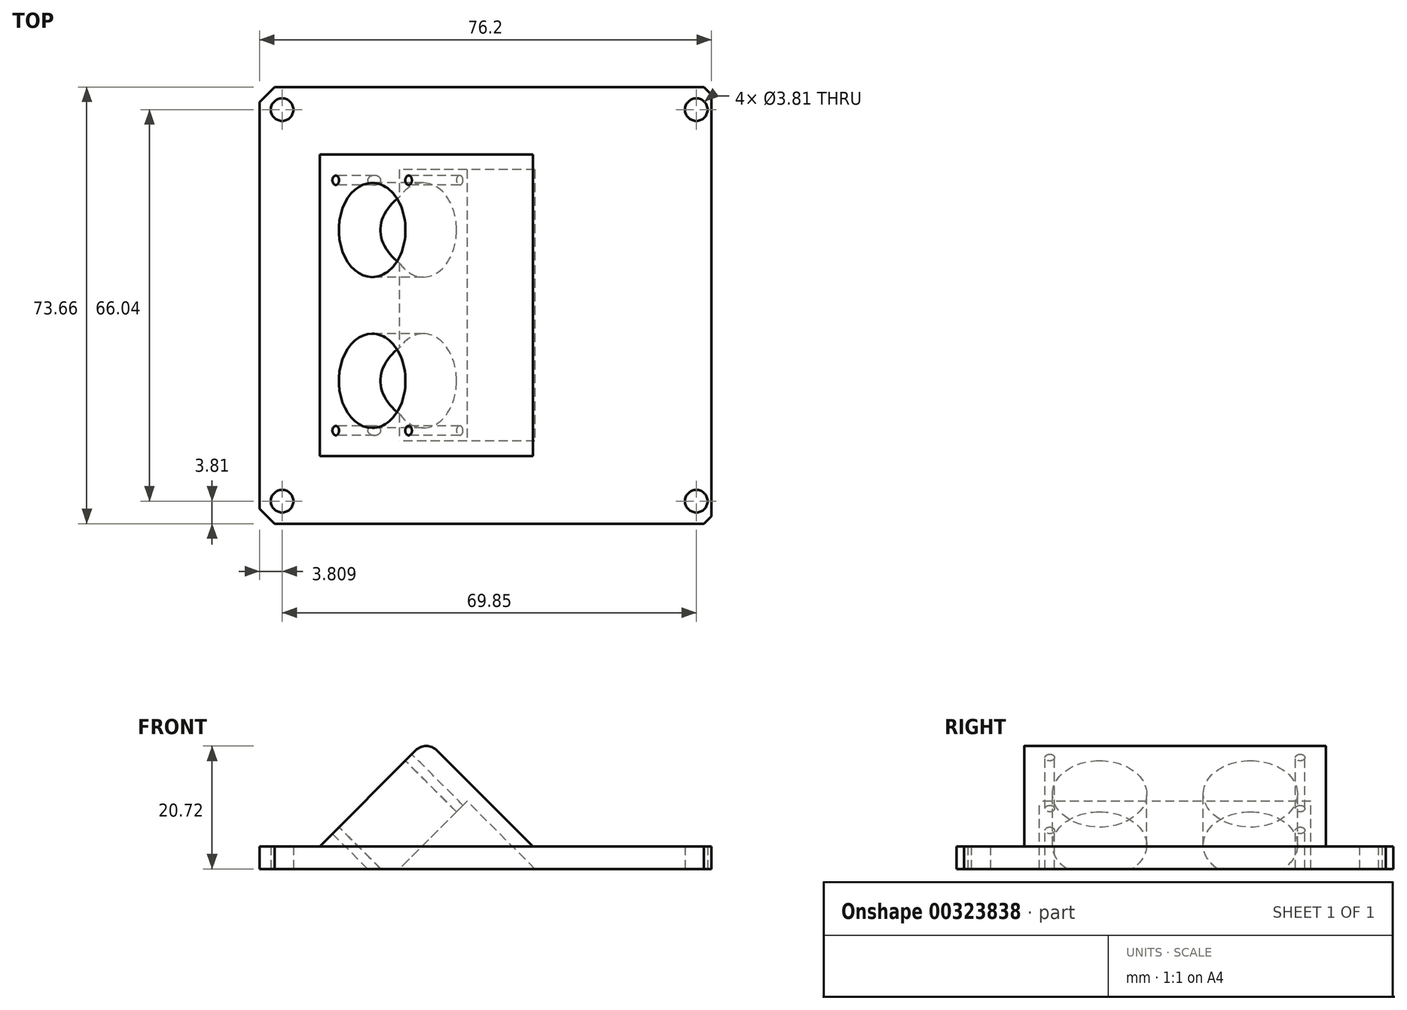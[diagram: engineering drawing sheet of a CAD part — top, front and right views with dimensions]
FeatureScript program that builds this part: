
annotation { "Feature Type Name" : "Feature", "Feature Type Description" : "" }
export const myFeature = defineFeature(function(context is Context, id is Id, definition is map)
    precondition{}
    {
        {
            var Q0;
            Q0=qCreatedBy(makeId("Top.planeOp"),FACE);
            var sketch = newSketch(context, id + "F0", { "sketchPlane" : qUnion([Q0])});
            skLineSegment(sketch, "E0.bottom", {"start": v(-80.1, 87.1) * mm, "end": v(-3.9, 87.1) * mm});
            skLineSegment(sketch, "E0.top", {"start": v(-80.1, 13.44) * mm, "end": v(-3.9, 13.44) * mm});
            skLineSegment(sketch, "E0.left", {"start": v(-80.1, 87.1) * mm, "end": v(-80.1, 13.44) * mm});
            skLineSegment(sketch, "E0.right", {"start": v(-3.9, 87.1) * mm, "end": v(-3.9, 13.44) * mm});
            skCircle(sketch, "E1", {"center": v(-76.28, 83.29) * mm, "radius": 1.9 * mm});
            skCircle(sketch, "E2", {"center": v(-6.43, 83.29) * mm, "radius": 1.9 * mm});
            skCircle(sketch, "E3", {"center": v(-6.43, 17.25) * mm, "radius": 1.9 * mm});
            skCircle(sketch, "E4", {"center": v(-76.28, 17.25) * mm, "radius": 1.9 * mm});
            skSolve(sketch);
        }
        {
            var Q0;
            Q0=makeQuery(id+"F0.imprint","IMPRINT",FACE,{"disambiguationData":[TD([[makeQuery(id+"F0.imprint","IMPRINT",EDGE,{"derivedFrom":sQuery(id+"F0.wireOp",EDGE,"E0.bottom")}),-1.0]])]});
            extrude(context, id + "F1", {"entities" : qUnion([Q0]), "depth" : 3.8 * mm});
        }
        {
            var Q0;
            Q0=makeQuery(id+"F1.opExtrude","SWEPT_EDGE",EDGE,{"disambiguationData":[OSD([sQuery(id+"F0.wireOp",EDGE,"E0.top"),sQuery(id+"F0.wireOp",EDGE,"E0.right")])]});
            var Q1;
            Q1=makeQuery(id+"F1.opExtrude","SWEPT_EDGE",EDGE,{"disambiguationData":[OSD([sQuery(id+"F0.wireOp",EDGE,"E0.bottom"),sQuery(id+"F0.wireOp",EDGE,"E0.right")])]});
            chamfer(context, id + "F2", {"entities" : qUnion([Q0, Q1]), "width" : 1.27 * mm, "tangentPropagation" : true});
        }
        {
            var Q0;
            Q0=makeQuery(id+"F1.opExtrude","SWEPT_EDGE",EDGE,{"disambiguationData":[OSD([sQuery(id+"F0.wireOp",EDGE,"E0.top"),sQuery(id+"F0.wireOp",EDGE,"E0.left")])]});
            var Q1;
            Q1=makeQuery(id+"F1.opExtrude","SWEPT_EDGE",EDGE,{"disambiguationData":[OSD([sQuery(id+"F0.wireOp",EDGE,"E0.bottom"),sQuery(id+"F0.wireOp",EDGE,"E0.left")])]});
            chamfer(context, id + "F3", {"entities" : qUnion([Q0, Q1]), "width" : 2.54 * mm, "tangentPropagation" : true});
        }
        {
            var Q0;
            Q0=makeQuery(id+"F1.opExtrude","SWEPT_FACE",FACE,{"disambiguationData":[OSD([sQuery(id+"F0.wireOp",EDGE,"E0.top")])]});
            var sketch = newSketch(context, id + "F4", { "sketchPlane" : qUnion([Q0])});
            skLineSegment(sketch, "E5", {"start": v(-69.93, 3.8) * mm, "end": v(-51.97, 21.77) * mm});
            skLineSegment(sketch, "E6", {"start": v(-51.97, 21.77) * mm, "end": v(-34, 3.8) * mm});
            skSolve(sketch);
        }
        {
            var Q0;
            {var subQ0=sQuery(id+"F4.wireOp",EDGE,"E5");Q0=makeQuery(id+"F4.imprint","IMPRINT",FACE,{"disambiguationData":[TD([[makeQuery(id+"F4.imprint","IMPRINT",EDGE,{"derivedFrom":subQ0}),-1.0]])]});}
            var Q1;
            Q1=makeQuery(id+"F1.opExtrude","SWEPT_FACE",FACE,{"disambiguationData":[OSD([sQuery(id+"F0.wireOp",EDGE,"E0.bottom")])]});
            extrude(context, id + "F5", {"entities" : qUnion([Q0]), "operationType" : NewBodyOperationType.ADD, "endBound" : BoundingType.UP_TO_SURFACE, "oppositeDirection" : true, "endBoundEntityFace" : qUnion([Q1]), "depth" : 25.4 * mm});
        }
        {
            var Q0;
            Q0=makeQuery(id+"F5.opExtrude","SWEPT_FACE",FACE,{"disambiguationData":[OSD([sQuery(id+"F4.wireOp",EDGE,"E5")])]});
            var sketch = newSketch(context, id + "F6", { "sketchPlane" : qUnion([Q0])});
            skCircle(sketch, "E7", {"center": v(-71.38, -25.57) * mm, "radius": 0.8 * mm});
            skCircle(sketch, "E8", {"center": v(-29.16, -25.57) * mm, "radius": 0.8 * mm});
            skCircle(sketch, "E9", {"center": v(-29.16, -42.94) * mm, "radius": 0.8 * mm});
            skCircle(sketch, "E10", {"center": v(-71.38, -42.94) * mm, "radius": 0.8 * mm});
            skCircle(sketch, "E11", {"center": v(-62.99, -34.26) * mm, "radius": 7.94 * mm});
            skCircle(sketch, "E12", {"center": v(-37.55, -34.26) * mm, "radius": 7.94 * mm});
            skSolve(sketch);
        }
        {
            var Q0;
            Q0=makeQuery(id+"F6.imprint","IMPRINT",FACE,{"disambiguationData":[TD([[makeQuery(id+"F6.imprint","IMPRINT",EDGE,{"derivedFrom":sQuery(id+"F6.wireOp",EDGE,"E11")}),1.0]])]});
            var Q1;
            Q1=makeQuery(id+"F6.imprint","IMPRINT",FACE,{"disambiguationData":[TD([[makeQuery(id+"F6.imprint","IMPRINT",EDGE,{"derivedFrom":sQuery(id+"F6.wireOp",EDGE,"E12")}),1.0]])]});
            var Q2;
            Q2=makeQuery(id+"F6.imprint","IMPRINT",FACE,{"disambiguationData":[TD([[makeQuery(id+"F6.imprint","IMPRINT",EDGE,{"derivedFrom":sQuery(id+"F6.wireOp",EDGE,"E8")}),1.0]])]});
            var Q3;
            Q3=makeQuery(id+"F6.imprint","IMPRINT",FACE,{"disambiguationData":[TD([[makeQuery(id+"F6.imprint","IMPRINT",EDGE,{"derivedFrom":sQuery(id+"F6.wireOp",EDGE,"E9")}),1.0]])]});
            var Q4;
            Q4=makeQuery(id+"F6.imprint","IMPRINT",FACE,{"disambiguationData":[TD([[makeQuery(id+"F6.imprint","IMPRINT",EDGE,{"derivedFrom":sQuery(id+"F6.wireOp",EDGE,"E10")}),1.0]])]});
            var Q5;
            Q5=makeQuery(id+"F6.imprint","IMPRINT",FACE,{"disambiguationData":[TD([[makeQuery(id+"F6.imprint","IMPRINT",EDGE,{"derivedFrom":sQuery(id+"F6.wireOp",EDGE,"E7")}),1.0]])]});
            extrude(context, id + "F7", {"entities" : qUnion([Q0, Q1, Q2, Q3, Q4, Q5]), "operationType" : NewBodyOperationType.REMOVE, "endBound" : BoundingType.THROUGH_ALL, "oppositeDirection" : true, "depth" : 25.4 * mm});
        }
        {
            var Q0;
            Q0=makeQuery(id+"F5.opExtrude","SWEPT_FACE",FACE,{"disambiguationData":[OSD([sQuery(id+"F4.wireOp",EDGE,"E5")])]});
            cPlane(context, id + "F8", {"entities" : qUnion([Q0]), "cplaneType" : CPlaneType.OFFSET, "offset" : 12.2 * mm, "oppositeDirection" : true, "width" : 152.4 * mm, "height" : 152.4 * mm});
        }
        {
            var Q0;
            Q0=qCreatedBy(id+"F8.planeOp",FACE);
            var sketch = newSketch(context, id + "F9", { "sketchPlane" : qUnion([Q0])});
            skCircle(sketch, "E13.0", {"center": v(-71.38, -25.57) * mm, "radius": 0.8 * mm});
            skCircle(sketch, "E14.0", {"center": v(-29.16, -25.57) * mm, "radius": 0.8 * mm});
            skCircle(sketch, "E15.0", {"center": v(-29.16, -42.94) * mm, "radius": 0.8 * mm});
            skCircle(sketch, "E16.0", {"center": v(-71.38, -42.94) * mm, "radius": 0.8 * mm});
            skLineSegment(sketch, "E17.bottom", {"start": v(-72.9, -24.05) * mm, "end": v(-27.63, -24.05) * mm});
            skLineSegment(sketch, "E17.top", {"start": v(-72.9, -44.47) * mm, "end": v(-27.63, -44.47) * mm});
            skLineSegment(sketch, "E17.left", {"start": v(-72.9, -24.05) * mm, "end": v(-72.9, -44.47) * mm});
            skLineSegment(sketch, "E17.right", {"start": v(-27.63, -24.05) * mm, "end": v(-27.63, -44.47) * mm});
            skLineSegment(sketch, "E18.0", {"start": v(-73.16, -23.8) * mm, "end": v(-27.38, -23.8) * mm});
            skLineSegment(sketch, "E18.1", {"start": v(-73.16, -23.8) * mm, "end": v(-73.16, -44.72) * mm});
            skLineSegment(sketch, "E18.2", {"start": v(-73.16, -44.72) * mm, "end": v(-27.38, -44.72) * mm});
            skLineSegment(sketch, "E18.3", {"start": v(-27.38, -23.8) * mm, "end": v(-27.38, -44.72) * mm});
            skSolve(sketch);
        }
        {
            var Q0;
            Q0=makeQuery(id+"F9.imprint","IMPRINT",FACE,{"disambiguationData":[TD([[makeQuery(id+"F9.imprint","IMPRINT",EDGE,{"derivedFrom":sQuery(id+"F9.wireOp",EDGE,"E17.bottom")}),1.0]])]});
            var Q1;
            Q1=makeQuery(id+"F9.imprint","IMPRINT",FACE,{"disambiguationData":[TD([[makeQuery(id+"F9.imprint","IMPRINT",EDGE,{"derivedFrom":sQuery(id+"F9.wireOp",EDGE,"E13.0")}),-1.0]])]});
            var Q2;
            Q2=makeQuery(id+"F9.imprint","IMPRINT",FACE,{"disambiguationData":[TD([[makeQuery(id+"F9.imprint","IMPRINT",EDGE,{"derivedFrom":sQuery(id+"F9.wireOp",EDGE,"E14.0")}),1.0]])]});
            var Q3;
            Q3=makeQuery(id+"F9.imprint","IMPRINT",FACE,{"disambiguationData":[TD([[makeQuery(id+"F9.imprint","IMPRINT",EDGE,{"derivedFrom":sQuery(id+"F9.wireOp",EDGE,"E15.0")}),1.0]])]});
            var Q4;
            Q4=makeQuery(id+"F9.imprint","IMPRINT",FACE,{"disambiguationData":[TD([[makeQuery(id+"F9.imprint","IMPRINT",EDGE,{"derivedFrom":sQuery(id+"F9.wireOp",EDGE,"E16.0")}),1.0]])]});
            var Q5;
            Q5=makeQuery(id+"F9.imprint","IMPRINT",FACE,{"disambiguationData":[TD([[makeQuery(id+"F9.imprint","IMPRINT",EDGE,{"derivedFrom":sQuery(id+"F9.wireOp",EDGE,"E13.0")}),1.0]])]});
            extrude(context, id + "F10", {"entities" : qUnion([Q0, Q1, Q2, Q3, Q4, Q5]), "operationType" : NewBodyOperationType.REMOVE, "oppositeDirection" : true, "depth" : 25.4 * mm});
        }
        {
            var Q0;
            Q0=makeQuery(id+"F1.opExtrude","SWEPT_FACE",FACE,{"disambiguationData":[OSD([sQuery(id+"F0.wireOp",EDGE,"E0.left")])]});
            var sketch = newSketch(context, id + "F11", { "sketchPlane" : qUnion([Q0])});
            skLineSegment(sketch, "E19.0", {"start": v(-73.16, 11.43) * mm, "end": v(-73.16, 0) * mm});
            skLineSegment(sketch, "E20.0", {"start": v(-27.38, 11.43) * mm, "end": v(-27.38, 0) * mm});
            skLineSegment(sketch, "E21", {"start": v(-94.18, 27.08) * mm, "end": v(-75.7, 27.08) * mm});
            skLineSegment(sketch, "E22", {"start": v(-75.7, 27.08) * mm, "end": v(-75.7, 3.81) * mm});
            skLineSegment(sketch, "E23", {"start": v(-75.7, 3.81) * mm, "end": v(-93.65, 3.81) * mm});
            skLineSegment(sketch, "E24", {"start": v(-93.65, 3.81) * mm, "end": v(-94.18, 27.08) * mm});
            skLineSegment(sketch, "E25", {"start": v(-50.27, 3.81) * mm, "end": v(-50.27, 21.74) * mm, "construction": true});
            skPoint(sketch, "E25.endSnap0", {"position": v(-50.27, 3.81) * mm});
            skLineSegment(sketch, "E26.MirrorCS", {"start": v(-6.36, 27.08) * mm, "end": v(-24.84, 27.08) * mm});
            skLineSegment(sketch, "E27.MirrorCS", {"start": v(-24.84, 27.08) * mm, "end": v(-24.84, 3.81) * mm});
            skLineSegment(sketch, "E28.MirrorCS", {"start": v(-24.84, 3.81) * mm, "end": v(-6.89, 3.81) * mm});
            skLineSegment(sketch, "E29.MirrorCS", {"start": v(-6.89, 3.81) * mm, "end": v(-6.36, 27.08) * mm});
            skSolve(sketch);
        }
        {
            var Q0;
            Q0=makeQuery(id+"F11.imprint","IMPRINT",FACE,{"disambiguationData":[TD([[makeQuery(id+"F11.imprint","IMPRINT",EDGE,{"derivedFrom":sQuery(id+"F11.wireOp",EDGE,"E21")}),-1.0]])]});
            var Q1;
            Q1=makeQuery(id+"F11.imprint","IMPRINT",FACE,{"disambiguationData":[TD([[makeQuery(id+"F11.imprint","IMPRINT",EDGE,{"derivedFrom":sQuery(id+"F11.wireOp",EDGE,"E26.MirrorCS")}),1.0]])]});
            extrude(context, id + "F12", {"entities" : qUnion([Q0, Q1]), "operationType" : NewBodyOperationType.REMOVE, "endBound" : BoundingType.THROUGH_ALL, "oppositeDirection" : true, "depth" : 25.4 * mm});
        }
        {
            var Q0;
            Q0=makeQuery(id+"F5.opExtrude","SWEPT_EDGE",EDGE,{"disambiguationData":[OSD([sQuery(id+"F4.wireOp",EDGE,"E5"),sQuery(id+"F4.wireOp",EDGE,"E6")])]});
            fillet(context, id + "F13", {"entities" : qUnion([Q0]), "radius" : 2.54 * mm, "tangentPropagation" : true, "allowEdgeOverflow" : false});
        }
    });
